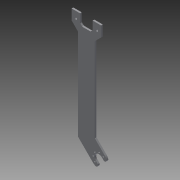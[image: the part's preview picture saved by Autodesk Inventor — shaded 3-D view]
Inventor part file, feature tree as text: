
AUTODESK INVENTOR PART (.ipt)
format: ipt  version: 2013 (Build 170138000, 138)  size: 190,976 bytes
history: native  units: mm
features: sketch x3, extrude x2, fillet x2, hole x1, pattern_circular x1
ambient origin geometry x8: Origin, YZ Plane, XZ Plane, XY Plane, X Axis, Y Axis, Z Axis, Center Point
feature tree (9):
  extrude  "押し出し2"  Depth=20.0mm
  hole  "穴1"  [1 undecoded]
  pattern_circular  "円形状パターン1"  Angle=135.0deg  [1 undecoded]
  extrude  "押し出し3"  TaperAngle=45.0deg  [1 undecoded]
  fillet  "フィレット1"  Radius=15.0mm
  fillet  "フィレット2"  Radius=2.5mm
  sketch  "スケッチ1"
  sketch  "スケッチ2"
  sketch  "スケッチ3"
note: 3 required parameter values undecoded (feature->parameter linkage not recoverable at this tier; creation-order binding heuristic only, values carry confidence <= 0.55)
